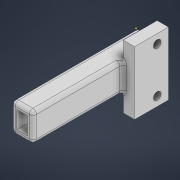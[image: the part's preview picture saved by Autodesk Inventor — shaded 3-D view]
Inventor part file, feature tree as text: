
AUTODESK INVENTOR PART (.ipt)
format: ipt  version: 2021 (Build 250183000, 183)  size: 316,928 bytes
history: native  units: mm
features: sketch x5, extrude x4, fillet x1
ambient origin geometry x8: Origin, YZ Plane, XZ Plane, XY Plane, X Axis, Y Axis, Z Axis, Center Point
bodies: Solid1 (feature_tree)
feature tree (10):
  extrude  "Extrusion1"  Depth=8.0mm
  sketch  "Sketch2"  dims[d2=35.0mm d3=0.0mm d4=4.95mm]
  extrude  "Extrusion2"  Depth=4.95mm
  extrude  "Extrusion3"  Depth=3.0mm
  extrude  "Extrusion4"  Depth=10.0mm
  fillet  "Fillet2"  Radius=10.0mm
  sketch  "Sketch1"  dims[d0=6.0mm d1=8.0mm]
  sketch  "Sketch3"  dims[d5=2.95mm d6=3.0mm]
  sketch  "Sketch4"  dims[d7=2.475mm d9=1.475mm d10=10.0mm d11=0.0mm]
  sketch  "Sketch5"  dims[d12=4.0mm d13=9.525mm d14=17.78mm d15=4.89mm d16=3.175mm d17=0.0mm d18=2.1844mm d19=2.1844mm d20=12.7mm d21=2.54mm d22=3.75mm d23=0.0mm d26=3.175mm d27=3.175mm d28=1.0mm]
